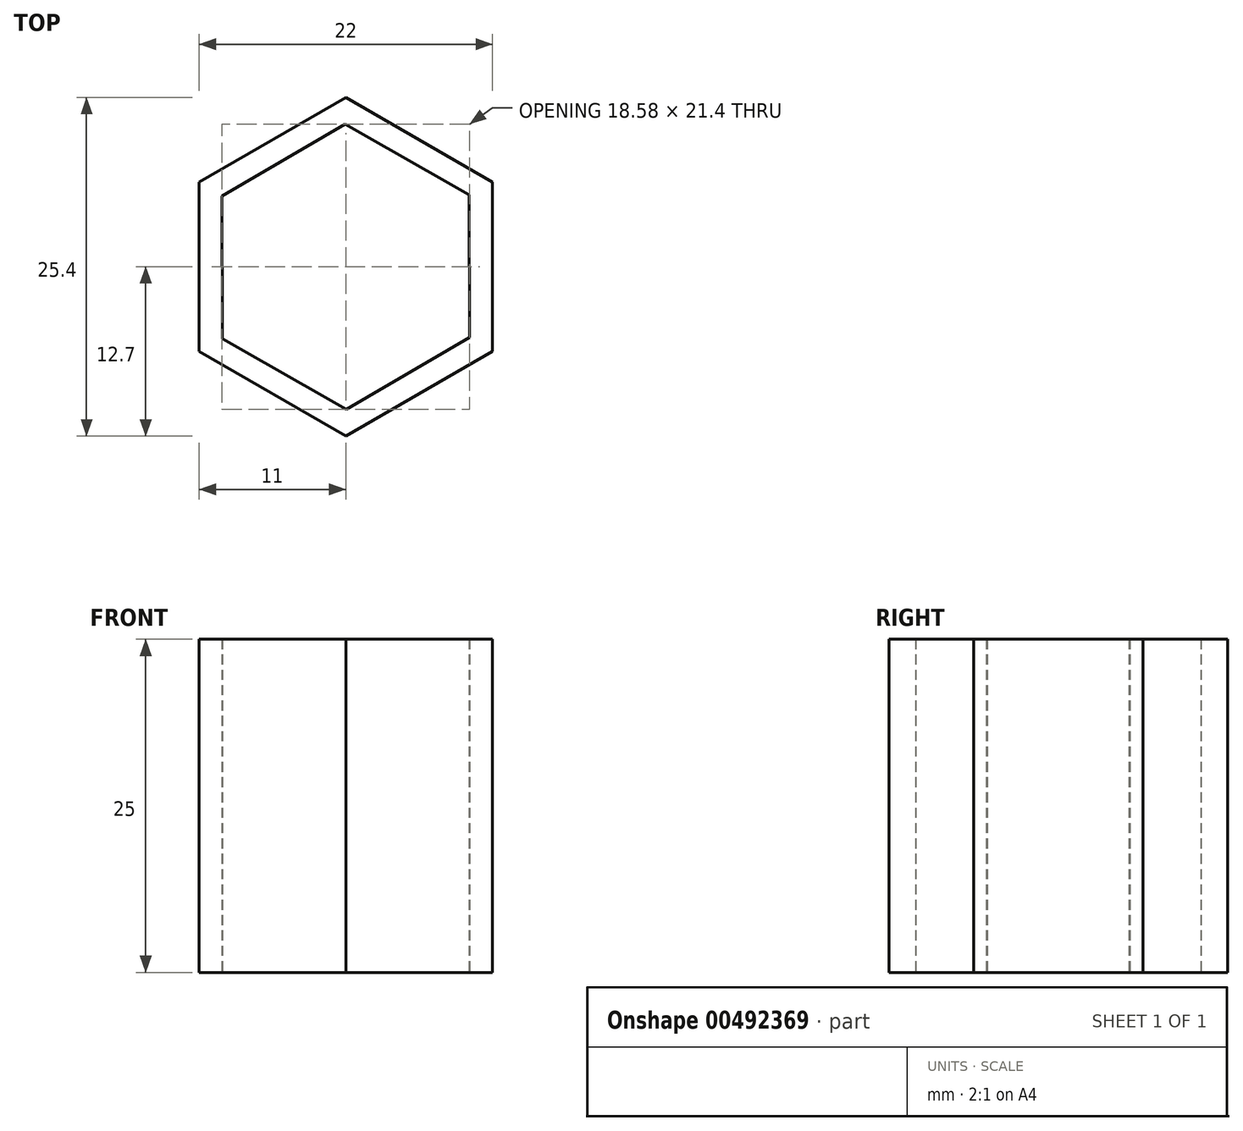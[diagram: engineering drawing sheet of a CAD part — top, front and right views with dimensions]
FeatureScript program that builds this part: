
annotation { "Feature Type Name" : "Feature", "Feature Type Description" : "" }
export const myFeature = defineFeature(function(context is Context, id is Id, definition is map)
    precondition{}
    {
        {
            var Q0;
            Q0=qCreatedBy(makeId("Top.planeOp"),FACE);
            var sketch = newSketch(context, id + "F0", { "sketchPlane" : qUnion([Q0])});
            skCircle(sketch, "E0.cCircle", {"center": v(0, 0) * mm, "radius": 11 * mm, "construction": true});
            skLineSegment(sketch, "E0.0", {"start": v(0, 12.7) * mm, "end": v(11, 6.35) * mm});
            skLineSegment(sketch, "E0.1", {"start": v(11, 6.35) * mm, "end": v(11, -6.35) * mm});
            skLineSegment(sketch, "E0.2", {"start": v(11, -6.35) * mm, "end": v(0, -12.7) * mm});
            skLineSegment(sketch, "E0.3", {"start": v(0, -12.7) * mm, "end": v(-11, -6.35) * mm});
            skLineSegment(sketch, "E0.4", {"start": v(-11, -6.35) * mm, "end": v(-11, 6.35) * mm});
            skLineSegment(sketch, "E0.5", {"start": v(-11, 6.35) * mm, "end": v(0, 12.7) * mm});
            skPoint(sketch, "E0.0.midPoint", {"position": v(5.5, 9.52) * mm});
            skSolve(sketch);
        }
        {
            var Q0;
            Q0=qSketchRegion(id+"F0",true);
            extrude(context, id + "F1", {"entities" : qUnion([Q0]), "depth" : 1 * mm});
        }
        {
            var Q0;
            Q0=qCreatedBy(makeId("Top.planeOp"),FACE);
            var sketch = newSketch(context, id + "F2", { "sketchPlane" : qUnion([Q0])});
            skCircle(sketch, "E1.cCircle", {"center": v(0, 0) * mm, "radius": 9.27 * mm, "construction": true});
            skLineSegment(sketch, "E1.0", {"start": v(-0.05, 10.7) * mm, "end": v(9.24, 5.39) * mm});
            skLineSegment(sketch, "E1.1", {"start": v(9.24, 5.39) * mm, "end": v(9.29, -5.31) * mm});
            skLineSegment(sketch, "E1.2", {"start": v(9.29, -5.31) * mm, "end": v(0.05, -10.7) * mm});
            skLineSegment(sketch, "E1.3", {"start": v(0.05, -10.7) * mm, "end": v(-9.24, -5.39) * mm});
            skLineSegment(sketch, "E1.4", {"start": v(-9.24, -5.39) * mm, "end": v(-9.29, 5.31) * mm});
            skLineSegment(sketch, "E1.5", {"start": v(-9.29, 5.31) * mm, "end": v(-0.05, 10.7) * mm});
            skPoint(sketch, "E1.0.midPoint", {"position": v(4.6, 8.05) * mm});
            skSolve(sketch);
        }
        {
            var Q0;
            Q0=qSketchRegion(id+"F2",true);
            extrude(context, id + "F3", {"entities" : qUnion([Q0]), "operationType" : NewBodyOperationType.REMOVE, "depth" : 1 * mm});
        }
        {
            var Q0;
            Q0=qCreatedBy(makeId("Top.planeOp"),FACE);
            var sketch = newSketch(context, id + "F4", { "sketchPlane" : qUnion([Q0])});
            skSolve(sketch);
        }
        {
            var Q0;
            Q0 = qSketchRegion(id + "F4", true);
            var Q1;
            Q1=makeQuery(id+"F1.opExtrude","CAP_FACE",FACE,{"disambiguationData":[OSD([sQuery(id+"F0.wireOp",EDGE,"E0.0"),sQuery(id+"F0.wireOp",EDGE,"E0.1"),sQuery(id+"F0.wireOp",EDGE,"E0.2"),sQuery(id+"F0.wireOp",EDGE,"E0.3"),sQuery(id+"F0.wireOp",EDGE,"E0.4"),sQuery(id+"F0.wireOp",EDGE,"E0.5")])],"isStart":false});
            extrude(context, id + "F5", {"entities" : qUnion([Q0, Q1]), "operationType" : NewBodyOperationType.ADD, "oppositeDirection" : true, "depth" : 25 * mm});
        }
    });
